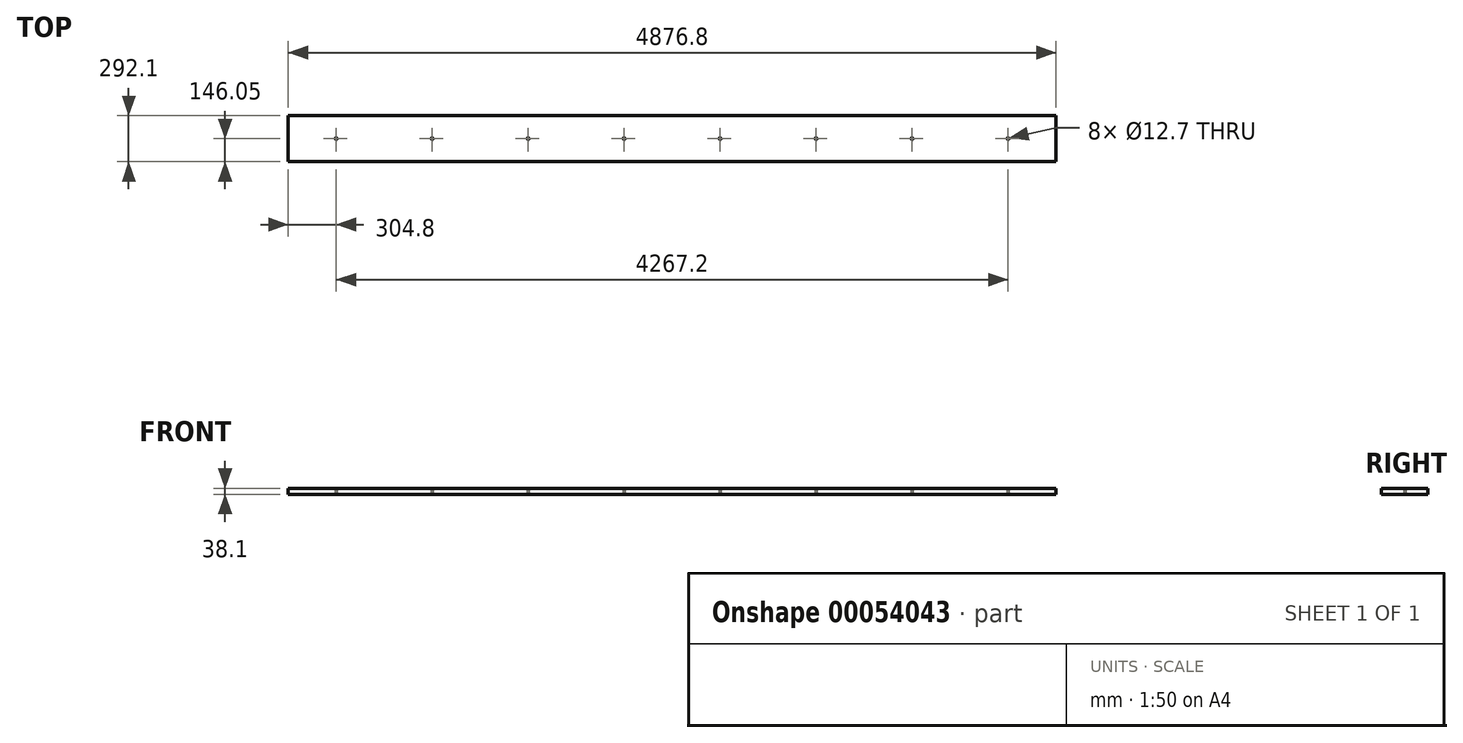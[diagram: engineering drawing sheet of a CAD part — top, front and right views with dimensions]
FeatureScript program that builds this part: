
annotation { "Feature Type Name" : "Feature", "Feature Type Description" : "" }
export const myFeature = defineFeature(function(context is Context, id is Id, definition is map)
    precondition{}
    {
        {
            var Q0;
            Q0=qCreatedBy(makeId("Right.planeOp"),FACE);
            var sketch = newSketch(context, id + "F0", { "sketchPlane" : qUnion([Q0])});
            skLineSegment(sketch, "E0.bottom", {"start": v(0, 0) * mm, "end": v(292.1, 0) * mm});
            skLineSegment(sketch, "E0.top", {"start": v(0, 38.1) * mm, "end": v(292.1, 38.1) * mm});
            skLineSegment(sketch, "E0.left", {"start": v(0, 0) * mm, "end": v(0, 38.1) * mm});
            skLineSegment(sketch, "E0.right", {"start": v(292.1, 0) * mm, "end": v(292.1, 38.1) * mm});
            skSolve(sketch);
        }
        {
            var Q0;
            Q0=makeQuery(id+"F0.imprint","IMPRINT",FACE,{"disambiguationData":[TD([[makeQuery(id+"F0.imprint","IMPRINT",EDGE,{"derivedFrom":sQuery(id+"F0.wireOp",EDGE,"E0.bottom")}),1.0]])]});
            extrude(context, id + "F1", {"entities" : qUnion([Q0]), "depth" : 4876.8 * mm});
        }
        {
            var Q0;
            Q0=makeQuery(id+"F1.opExtrude","SWEPT_FACE",FACE,{"disambiguationData":[OSD([sQuery(id+"F0.wireOp",EDGE,"E0.bottom")])]});
            var sketch = newSketch(context, id + "F2", { "sketchPlane" : qUnion([Q0])});
            skLineSegment(sketch, "E1", {"start": v(0, -146.05) * mm, "end": v(9448.8, -146.05) * mm, "construction": true});
            skPoint(sketch, "E1.endSnap0", {"position": v(4876.8, -146.05) * mm});
            skCircle(sketch, "E2", {"center": v(304.8, -146.05) * mm, "radius": 6.35 * mm});
            skCircle(sketch, "E3", {"center": v(914.4, -146.05) * mm, "radius": 6.35 * mm});
            skCircle(sketch, "E4", {"center": v(1524, -146.05) * mm, "radius": 6.35 * mm});
            skCircle(sketch, "E5", {"center": v(3962.4, -146.05) * mm, "radius": 6.35 * mm});
            skCircle(sketch, "E6", {"center": v(2133.6, -146.05) * mm, "radius": 6.35 * mm});
            skCircle(sketch, "E7", {"center": v(2743.2, -146.05) * mm, "radius": 6.35 * mm});
            skCircle(sketch, "E8", {"center": v(3352.8, -146.05) * mm, "radius": 6.35 * mm});
            skCircle(sketch, "E9", {"center": v(4572, -146.05) * mm, "radius": 6.35 * mm});
            skSolve(sketch);
        }
        {
            var Q0;
            Q0 = qSketchRegion(id + "F2", true);
            extrude(context, id + "F3", {"entities" : qUnion([Q0]), "operationType" : NewBodyOperationType.REMOVE, "endBound" : BoundingType.THROUGH_ALL, "oppositeDirection" : true, "depth" : 25.4 * mm});
        }
    });
